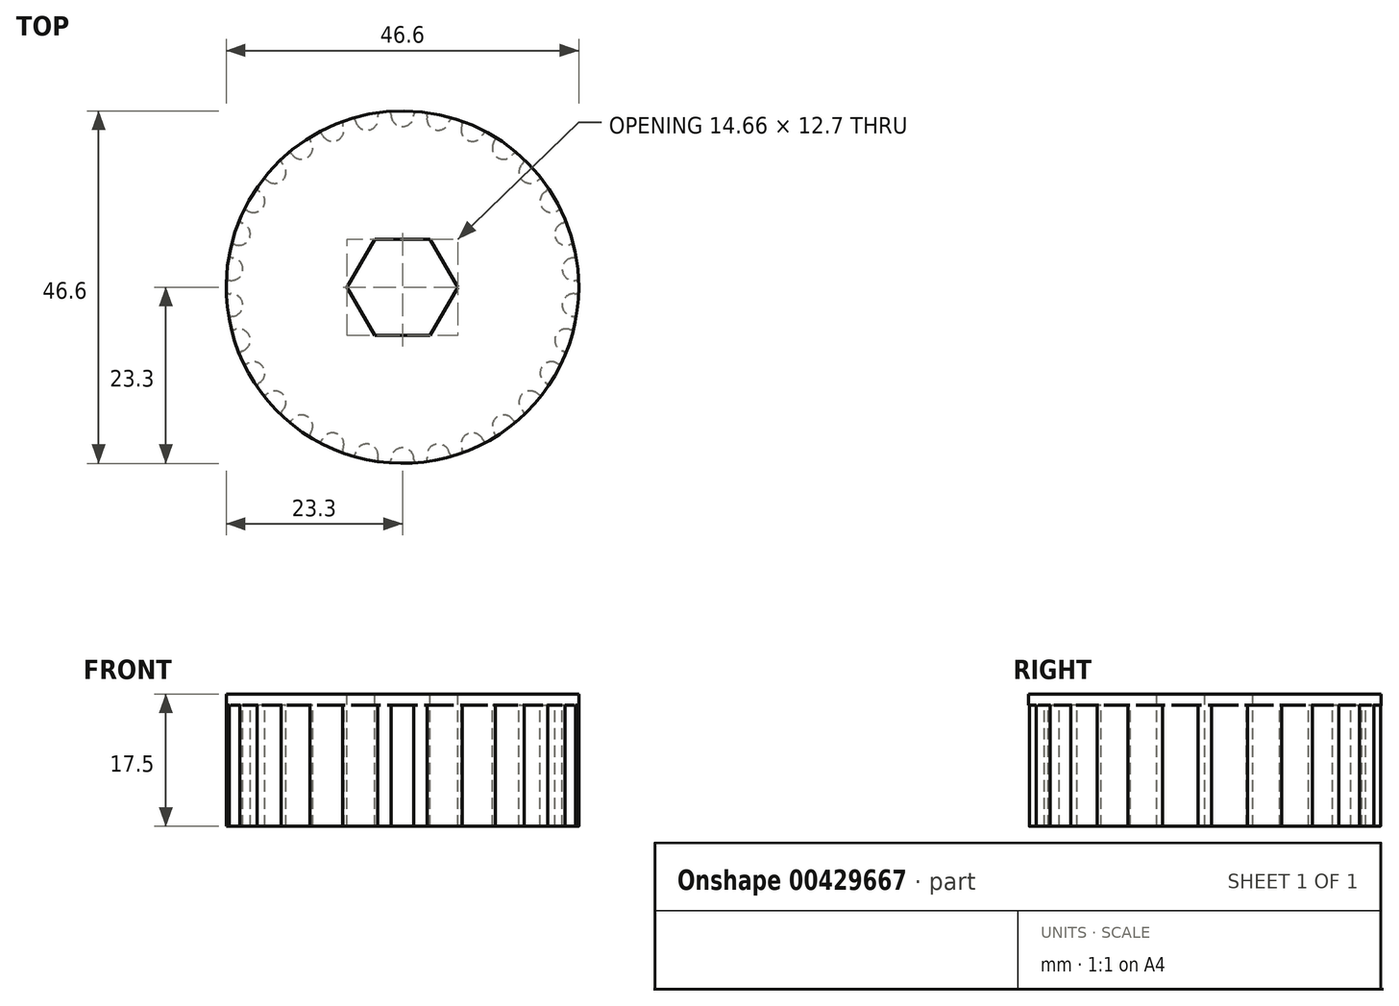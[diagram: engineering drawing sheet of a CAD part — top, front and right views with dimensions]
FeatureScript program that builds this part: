
annotation { "Feature Type Name" : "Feature", "Feature Type Description" : "" }
export const myFeature = defineFeature(function(context is Context, id is Id, definition is map)
    precondition{}
    {
        {
            assignVariable(context, id + "F0", {"name" : "Teeth", "anyValue" : 30});
        }
        {
            assignVariable(context, id + "F1", {"name" : "Width", "anyValue" : 16});
        }
        {
            var Q0;
            Q0=qCreatedBy(makeId("Top.planeOp"),FACE);
            var sketch = newSketch(context, id + "F2", { "sketchPlane" : qUnion([Q0])});
            skCircle(sketch, "E0", {"center": v(0, 0) * mm, "radius": 23.3 * mm});
            skSolve(sketch);
        }
        {
            var Q0;
            Q0=qSketchRegion(id+"F2",true);
            extrude(context, id + "F3", {"entities" : qUnion([Q0]), "depth" : (getVariable(context, 'Width')) * mm});
        }
        {
            var Q0;
            Q0=makeQuery(id+"F3.opExtrude","CAP_FACE",FACE,{"disambiguationData":[OSD([sQuery(id+"F2.wireOp",EDGE,"E0")])],"isStart":false});
            var sketch = newSketch(context, id + "F4", { "sketchPlane" : qUnion([Q0])});
            skCircle(sketch, "E1", {"center": v(0, 0) * mm, "radius": 21.24 * mm, "construction": true});
            skArc(sketch, "E2", {"start": v(-1.5, 22.76) * mm, "mid": v(0, 21.24) * mm, "end": v(1.5, 22.76) * mm});
            skArc(sketch, "E3", {"start": v(1.99, 23.22) * mm, "mid": v(0, 23.3) * mm, "end": v(-1.99, 23.22) * mm});
            skArc(sketch, "E4", {"start": v(-1.5, 22.76) * mm, "mid": v(-1.64, 23.1) * mm, "end": v(-1.99, 23.22) * mm});
            skArc(sketch, "E5", {"start": v(1.99, 23.22) * mm, "mid": v(1.64, 23.1) * mm, "end": v(1.5, 22.76) * mm});
            skSolve(sketch);
        }
        {
            var Q0;
            Q0=makeQuery(id+"F4.imprint","IMPRINT",FACE,{"disambiguationData":[TD([[makeQuery(id+"F4.imprint","IMPRINT",EDGE,{"derivedFrom":sQuery(id+"F4.wireOp",EDGE,"E2")}),1.0]])]});
            var Q1;
            Q1=makeQuery(id+"F3.opExtrude","CAP_FACE",FACE,{"disambiguationData":[OSD([sQuery(id+"F2.wireOp",EDGE,"E0")])],"isStart":true});
            extrude(context, id + "F5", {"entities" : qUnion([Q0]), "operationType" : NewBodyOperationType.REMOVE, "endBound" : BoundingType.UP_TO_SURFACE, "oppositeDirection" : true, "endBoundEntityFace" : qUnion([Q1]), "depth" : 25 * mm});
        }
        {
            var Q0;
            Q0=makeQuery(id+"F5.boolean.opBoolean","COPY",FACE,{"derivedFrom":makeQuery(id+"F5.opExtrude","SWEPT_FACE",FACE,{"disambiguationData":[OSD([sQuery(id+"F4.wireOp",EDGE,"E4")])]})});
            var Q1;
            Q1=makeQuery(id+"F5.boolean.opBoolean","COPY",FACE,{"derivedFrom":makeQuery(id+"F5.opExtrude","SWEPT_FACE",FACE,{"disambiguationData":[OSD([sQuery(id+"F4.wireOp",EDGE,"kHu0Iwj9-o4Cv-DRlk-4OjM-lw9Y4UkXsprA")])]})});
            var Q2;
            Q2=makeQuery(id+"F5.boolean.opBoolean","COPY",FACE,{"derivedFrom":makeQuery(id+"F5.opExtrude","SWEPT_FACE",FACE,{"disambiguationData":[OSD([sQuery(id+"F4.wireOp",EDGE,"E2")])]})});
            var Q3;
            Q3=makeQuery(id+"F5.boolean.opBoolean","COPY",FACE,{"derivedFrom":makeQuery(id+"F5.opExtrude","SWEPT_FACE",FACE,{"disambiguationData":[OSD([sQuery(id+"F4.wireOp",EDGE,"lCBZwTSR-BtAH-iuKv-YoZ4-wjcx4KIexOll")])]})});
            var Q4;
            Q4=makeQuery(id+"F5.boolean.opBoolean","COPY",FACE,{"derivedFrom":makeQuery(id+"F5.opExtrude","SWEPT_FACE",FACE,{"disambiguationData":[OSD([sQuery(id+"F4.wireOp",EDGE,"E5")])]})});
            var Q5;
            Q5=makeQuery(id+"F3.opExtrude","SWEPT_FACE",FACE,{"disambiguationData":[OSD([sQuery(id+"F2.wireOp",EDGE,"E0")])]});
            circularPattern(context, id + "F6", {"faces" : qUnion([Q0, Q1, Q2, Q3, Q4]), "axis" : qUnion([Q5]), "angle" : 360 * degree, "instanceCount" : getVariable(context, 'Teeth'), "equalSpace" : true, "patternType" : PatternType.FACE});
        }
        {
            var Q0;
            Q0=makeQuery(id+"F3.opExtrude","CAP_FACE",FACE,{"disambiguationData":[OSD([sQuery(id+"F2.wireOp",EDGE,"E0")])],"isStart":false});
            var sketch = newSketch(context, id + "F7", { "sketchPlane" : qUnion([Q0])});
            skCircle(sketch, "E6.0", {"center": v(0, 0) * mm, "radius": 23.3 * mm});
            skSolve(sketch);
        }
        {
            var Q0;
            Q0=qSketchRegion(id+"F7",true);
            extrude(context, id + "F8", {"entities" : qUnion([Q0]), "operationType" : NewBodyOperationType.ADD, "depth" : 1.5 * mm});
        }
        {
            var Q0;
            Q0=makeQuery(id+"F8.opExtrude","CAP_FACE",FACE,{"disambiguationData":[OSD([sQuery(id+"F7.wireOp",EDGE,"E6.0")])],"isStart":false});
            var sketch = newSketch(context, id + "F9", { "sketchPlane" : qUnion([Q0])});
            skCircle(sketch, "E7.cCircle", {"center": v(0, 0) * mm, "radius": 6.35 * mm, "construction": true});
            skLineSegment(sketch, "E7.0", {"start": v(3.67, -6.35) * mm, "end": v(-3.67, -6.35) * mm});
            skLineSegment(sketch, "E7.1", {"start": v(-3.67, -6.35) * mm, "end": v(-7.33, 0) * mm});
            skLineSegment(sketch, "E7.2", {"start": v(-7.33, 0) * mm, "end": v(-3.67, 6.35) * mm});
            skLineSegment(sketch, "E7.3", {"start": v(-3.67, 6.35) * mm, "end": v(3.67, 6.35) * mm});
            skLineSegment(sketch, "E7.4", {"start": v(3.67, 6.35) * mm, "end": v(7.33, 0) * mm});
            skLineSegment(sketch, "E7.5", {"start": v(7.33, 0) * mm, "end": v(3.67, -6.35) * mm});
            skPoint(sketch, "E7.0.midPoint", {"position": v(0, -6.35) * mm});
            skSolve(sketch);
        }
        {
            var Q0;
            Q0=makeQuery(id+"F9.imprint","IMPRINT",FACE,{"disambiguationData":[TD([[makeQuery(id+"F9.imprint","IMPRINT",EDGE,{"derivedFrom":sQuery(id+"F9.wireOp",EDGE,"E7.0")}),-1.0]])]});
            extrude(context, id + "F10", {"entities" : qUnion([Q0]), "operationType" : NewBodyOperationType.REMOVE, "endBound" : BoundingType.THROUGH_ALL, "oppositeDirection" : true, "depth" : 25 * mm});
        }
    });
